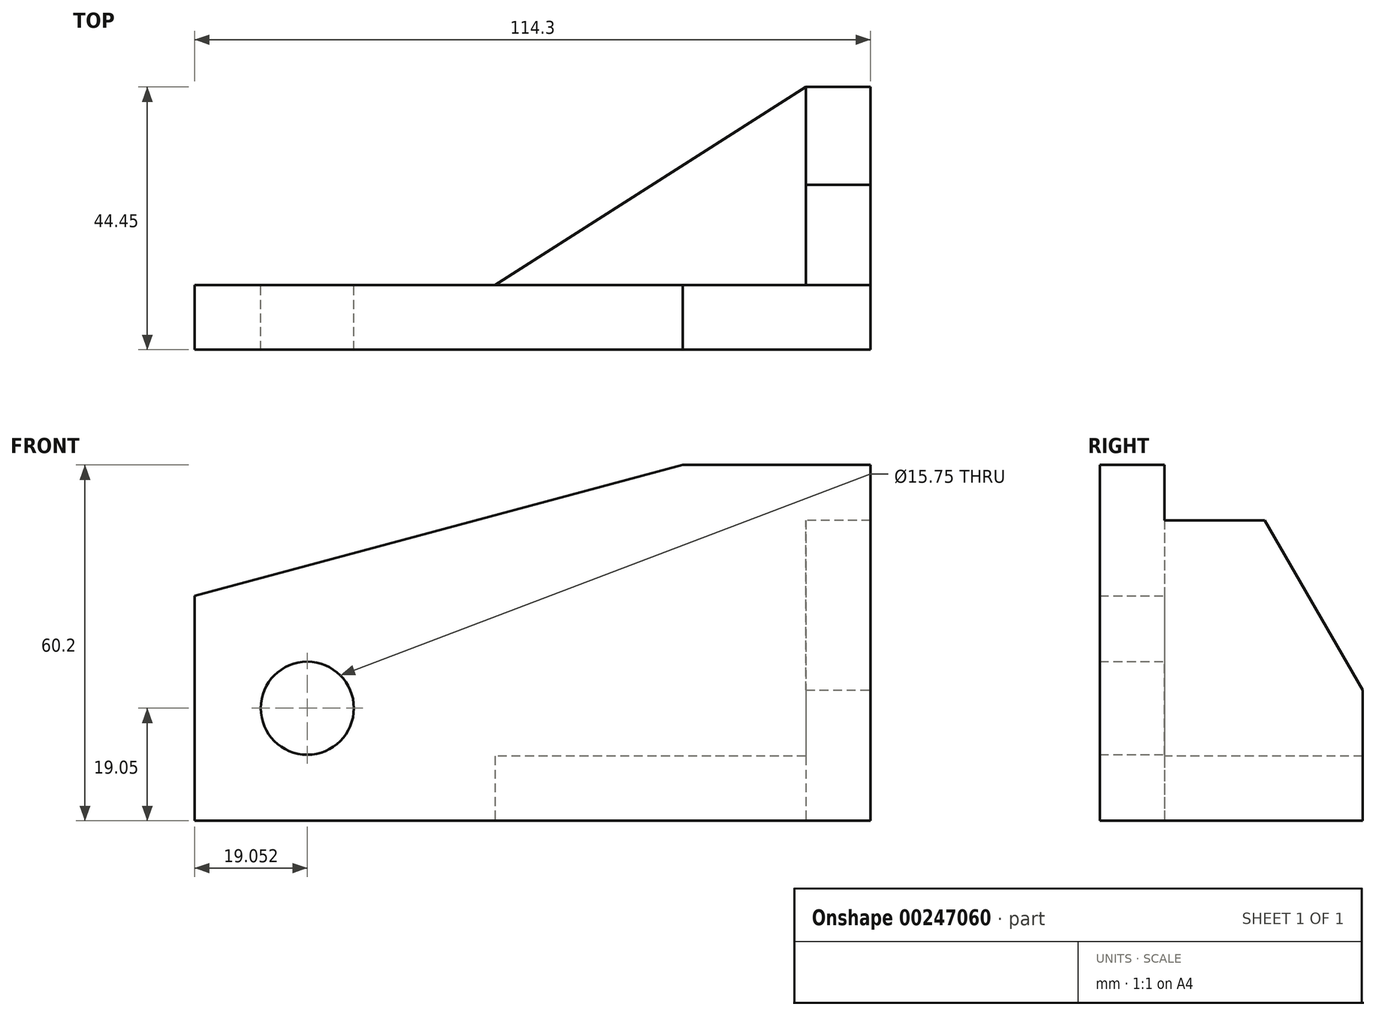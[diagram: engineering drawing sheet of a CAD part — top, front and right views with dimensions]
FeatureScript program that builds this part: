
annotation { "Feature Type Name" : "Feature", "Feature Type Description" : "" }
export const myFeature = defineFeature(function(context is Context, id is Id, definition is map)
    precondition{}
    {
        {
            var Q0;
            Q0=qCreatedBy(makeId("Top.planeOp"),FACE);
            var sketch = newSketch(context, id + "F0", { "sketchPlane" : qUnion([Q0])});
            skLineSegment(sketch, "E0", {"start": v(0, 0) * mm, "end": v(-52.58, 0) * mm});
            skLineSegment(sketch, "E1", {"start": v(0, 0) * mm, "end": v(0, 33.53) * mm});
            skLineSegment(sketch, "E2", {"start": v(0, 33.53) * mm, "end": v(-52.58, 0) * mm});
            skLineSegment(sketch, "E3.bottom", {"start": v(0, 33.53) * mm, "end": v(10.92, 33.53) * mm});
            skLineSegment(sketch, "E3.top", {"start": v(0, 0) * mm, "end": v(10.92, 0) * mm});
            skLineSegment(sketch, "E3.left", {"start": v(0, 33.53) * mm, "end": v(0, 0) * mm});
            skLineSegment(sketch, "E3.right", {"start": v(10.92, 33.53) * mm, "end": v(10.92, 0) * mm});
            skLineSegment(sketch, "E4.bottom", {"start": v(10.92, 0) * mm, "end": v(-103.38, 0) * mm});
            skLineSegment(sketch, "E4.top", {"start": v(10.92, -10.92) * mm, "end": v(-103.38, -10.92) * mm});
            skLineSegment(sketch, "E4.left", {"start": v(10.92, 0) * mm, "end": v(10.92, -10.92) * mm});
            skLineSegment(sketch, "E4.right", {"start": v(-103.38, 0) * mm, "end": v(-103.38, -10.92) * mm});
            skLineSegment(sketch, "E5", {"start": v(10.92, -10.92) * mm, "end": v(-20.83, -10.92) * mm});
            skLineSegment(sketch, "E6", {"start": v(-20.83, -10.92) * mm, "end": v(-20.83, 0) * mm});
            skSolve(sketch);
        }
        {
            var Q0;
            {var subQ0=sQuery(id+"F0.wireOp",EDGE,"E2");Q0=makeQuery(id+"F0.imprint","IMPRINT",FACE,{"disambiguationData":[TD([[makeQuery(id+"F0.imprint","IMPRINT",EDGE,{"derivedFrom":subQ0}),1.0]])]});}
            extrude(context, id + "F1", {"entities" : qUnion([Q0]), "depth" : 10.92 * mm});
        }
        {
            var Q0;
            Q0=makeQuery(id+"F0.imprint","IMPRINT",FACE,{"disambiguationData":[TD([[makeQuery(id+"F0.imprint","IMPRINT",EDGE,{"derivedFrom":sQuery(id+"F0.wireOp",EDGE,"E3.bottom")}),-1.0]])]});
            extrude(context, id + "F2", {"entities" : qUnion([Q0]), "operationType" : NewBodyOperationType.ADD, "depth" : 22.1 * mm});
        }
        {
            var Q0;
            Q0=qCreatedBy(makeId("Right.planeOp"),FACE);
            var sketch = newSketch(context, id + "F3", { "sketchPlane" : qUnion([Q0])});
            skLineSegment(sketch, "E7", {"start": v(0, 0) * mm, "end": v(0, 22.1) * mm});
            skLineSegment(sketch, "E8", {"start": v(0, 22.1) * mm, "end": v(33.53, 22.1) * mm});
            skLineSegment(sketch, "E9", {"start": v(0, 22.1) * mm, "end": v(0, 50.8) * mm});
            skLineSegment(sketch, "E10", {"start": v(0, 50.8) * mm, "end": v(16.96, 50.8) * mm});
            skLineSegment(sketch, "E11", {"start": v(33.53, 22.1) * mm, "end": v(16.96, 50.8) * mm});
            skPoint(sketch, "E12.orphan", {"position": v(33.53, 50.8) * mm});
            skSolve(sketch);
        }
        {
            var Q0;
            Q0=makeQuery(id+"F3.imprint","IMPRINT",FACE,{"disambiguationData":[TD([[makeQuery(id+"F3.imprint","IMPRINT",EDGE,{"derivedFrom":sQuery(id+"F3.wireOp",EDGE,"E8")}),1.0]])]});
            extrude(context, id + "F4", {"entities" : qUnion([Q0]), "operationType" : NewBodyOperationType.ADD, "depth" : 10.92 * mm});
        }
        {
            var Q0;
            Q0=qCreatedBy(makeId("Front.planeOp"),FACE);
            var sketch = newSketch(context, id + "F5", { "sketchPlane" : qUnion([Q0])});
            skLineSegment(sketch, "E13", {"start": v(0, 0) * mm, "end": v(0, 60.2) * mm});
            skLineSegment(sketch, "E14", {"start": v(0, 60.2) * mm, "end": v(10.92, 60.2) * mm});
            skLineSegment(sketch, "E15", {"start": v(10.92, 60.2) * mm, "end": v(-20.83, 60.2) * mm});
            skLineSegment(sketch, "E16", {"start": v(-20.83, 60.2) * mm, "end": v(-103.38, 60.2) * mm});
            skLineSegment(sketch, "E17", {"start": v(-103.38, 60.2) * mm, "end": v(-103.38, 0) * mm});
            skLineSegment(sketch, "E18", {"start": v(-20.83, 60.2) * mm, "end": v(-103.38, 38.08) * mm});
            skLineSegment(sketch, "E19", {"start": v(-103.38, 0) * mm, "end": v(-103.38, 0) * mm});
            skLineSegment(sketch, "E20", {"start": v(-103.38, 0) * mm, "end": v(-84.33, 0) * mm});
            skLineSegment(sketch, "E21", {"start": v(-84.33, 0) * mm, "end": v(-84.33, 19.05) * mm});
            skCircle(sketch, "E22", {"center": v(-84.33, 19.05) * mm, "radius": 7.87 * mm});
            skLineSegment(sketch, "E23", {"start": v(10.92, 60.2) * mm, "end": v(10.92, 0) * mm});
            skLineSegment(sketch, "E24", {"start": v(10.92, 0) * mm, "end": v(-84.33, 0) * mm});
            skSolve(sketch);
        }
        {
            var Q0;
            {var subQ0=sQuery(id+"F5.wireOp",EDGE,"E13");Q0=makeQuery(id+"F5.imprint","IMPRINT",FACE,{"disambiguationData":[TD([[makeQuery(id+"F5.imprint","IMPRINT",EDGE,{"derivedFrom":subQ0}),-1.0]])]});}
            var Q1;
            {var subQ4=sQuery(id+"F5.wireOp",EDGE,"E13");Q1=makeQuery(id+"F5.imprint","IMPRINT",FACE,{"disambiguationData":[TD([[makeQuery(id+"F5.imprint","IMPRINT",EDGE,{"derivedFrom":subQ4}),1.0]])]});}
            extrude(context, id + "F6", {"entities" : qUnion([Q0, Q1]), "operationType" : NewBodyOperationType.ADD, "depth" : 10.92 * mm});
        }
    });
